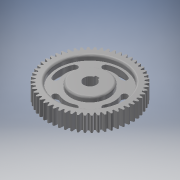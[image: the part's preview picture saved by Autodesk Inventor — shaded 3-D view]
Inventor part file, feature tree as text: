
AUTODESK INVENTOR PART (.ipt)
format: ipt  version: 2018 (Build 220112000, 112)  size: 807,936 bytes
history: native  units: mm (DEFAULTED — no unit token found)
features: sketch x6, extrude x5, plane x4, other x3, mirror x2, projected_geometry x2, fillet x1
ambient origin geometry x8: Origin, YZ Plane, XZ Plane, XY Plane, X Axis, Y Axis, Z Axis, Center Point
bodies: Body1 (feature_tree), Body2 (feature_tree)
feature tree (23):
  extrude  "Extrusion1"  Depth=30.0mm TaperAngle=0.0deg
  plane  "Work Plane2"
  plane  "Work Plane8"
  plane  "Work Plane9"
  other  "Engranaje recto"
  extrude  "Extrusión2"  Depth=10.0mm TaperAngle=0.0deg
  extrude  "Extrusión3"  Depth=0.581776mm TaperAngle=0.0deg
  extrude  "Extrusion4"  TaperAngle=0.0deg  [1 undecoded]
  fillet  "Fillet2"  Radius=108.0mm
  plane  "Work Plane11"
  mirror  "Mirror1"
  mirror  "Mirror2"
  extrude  "Extrusion5"  TaperAngle=0.0deg  [1 undecoded]
  sketch  "Sketch1"  dims[d0=168.0mm d1=30.0mm d2=0.0mm]
  sketch  "Sketch2"  dims[d3=162.0mm d4=10.0mm d5=0.0mm]
  other  "Srf1"
  sketch  "Boceto3"  dims[d16=108.0mm d17=0.0mm d34=0.581776mm]
  sketch  "Boceto4"  dims[d39=0.0mm d41=0.0mm d43=108.0mm]
  projected_geometry  "Contorno proyectado1"
  sketch  "Sketch5"  dims[d46=108.0mm d47=0.0mm d48=0.0mm]
  projected_geometry  "Projected Loop2"
  sketch  "Sketch6"  dims[d49=25.0mm d50=10.0mm d51=0.0mm d52=8.0mm d53=6.0mm d54=10.0mm d55=0.0mm d56=130.0mm d57=75.0mm d58=10.0mm d59=0.0mm d61=4.0mm d62=8.0mm d63=0.0mm]
  other  "Diámetro de separación"
note: 2 required parameter values undecoded (feature->parameter linkage not recoverable at this tier; creation-order binding heuristic only, values carry confidence <= 0.55)
